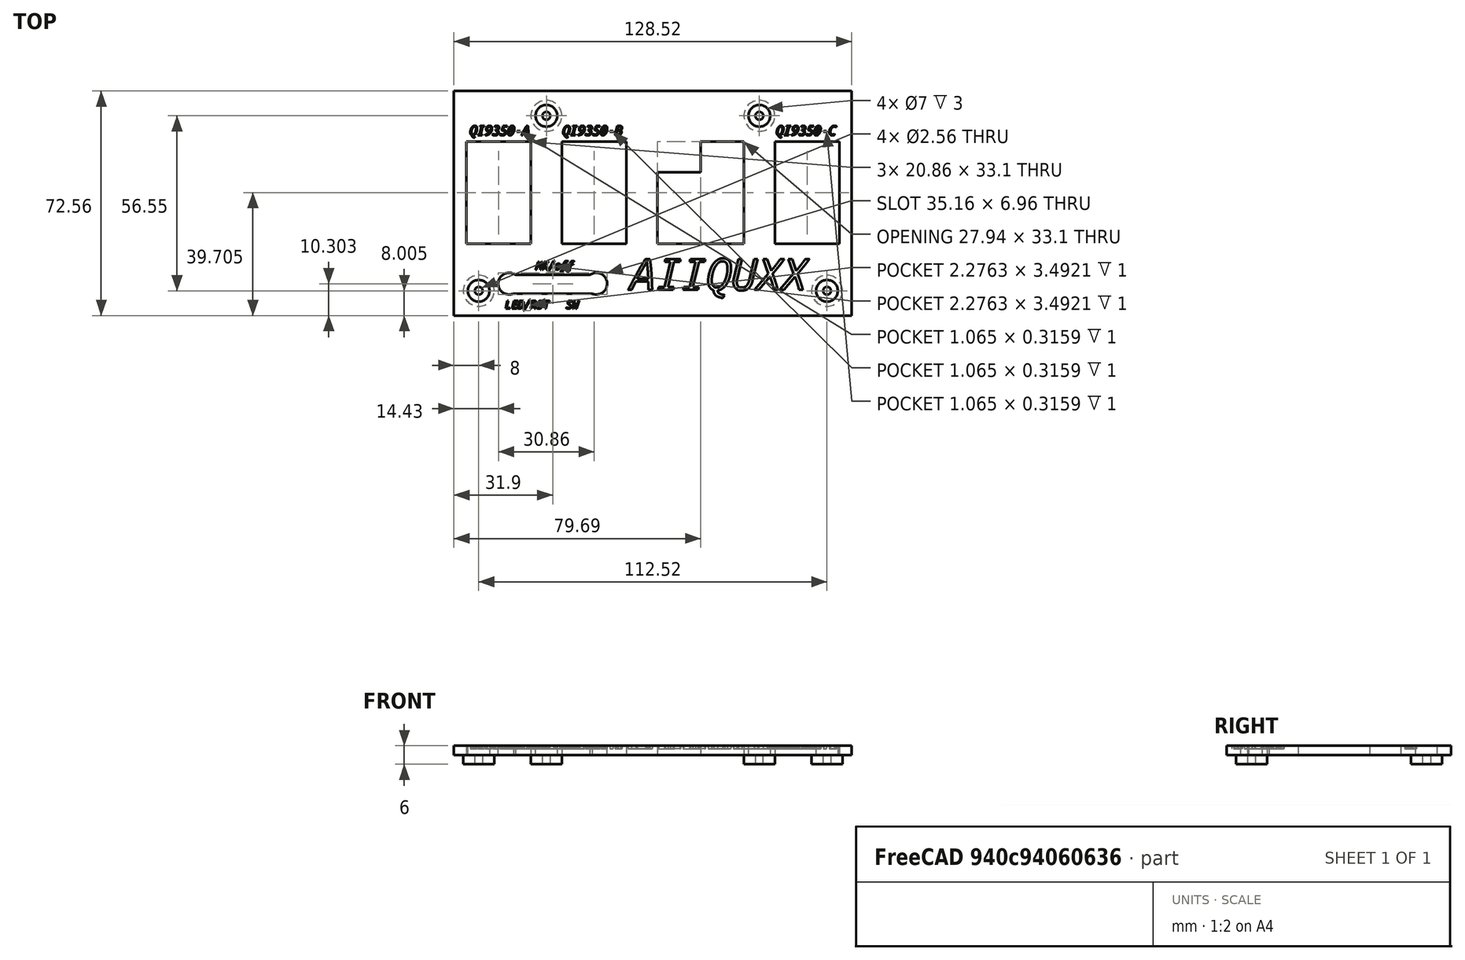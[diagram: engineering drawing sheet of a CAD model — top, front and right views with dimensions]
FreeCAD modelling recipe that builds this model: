
FCSTD DOCUMENT  (FreeCAD 1.0R38641 +678 (Git))
Label: box_cover_1
License: All rights reserved
LicenseURL: https://en.wikipedia.org/wiki/All_rights_reserved
objects: PartDesign::Pocket×9, Part::Part2DObjectPython×7, Sketcher::SketchObject×4, PartDesign::Pad×2, PartDesign::CoordinateSystem×1, PartDesign::Body×1, Mesh::Feature×1
note: 50 computed .brp shape members not serialized (recipe doc carries the construction recipe); baked Part::Feature solids carry a one-line shape summary decoded from their .brp

FEATURE [Sketcher::SketchObject] Sketch
  ArcFitTolerance = 1e-06
  AttachmentSupport = -> [XY_Plane]
  FullyConstrained = true
  MakeInternals = false
  MapMode = 5
  sketch-geometry (4):
    g0: LineSegment StartX=-64.26 StartY=-36.275 StartZ=0 EndX=64.26 EndY=-36.275 EndZ=0
    g1: LineSegment StartX=64.26 StartY=-36.275 StartZ=0 EndX=64.26 EndY=36.275 EndZ=0
    g2: LineSegment StartX=64.26 StartY=36.275 StartZ=0 EndX=-64.26 EndY=36.275 EndZ=0
    g3: LineSegment StartX=-64.26 StartY=36.275 StartZ=0 EndX=-64.26 EndY=-36.275 EndZ=0
  constraints (12):
    c: Coincident(g0,g1)
    c: Coincident(g1,g2)
    c: Coincident(g2,g3)
    c: Coincident(g3,g0)
    c: Horizontal(g0)
    c: Horizontal(g2)
    c: Vertical(g1)
    c: Vertical(g3)
    c: DistanceX(g2,g2) = 128.52
    c: DistanceX(g-1,g1) = 64.26
    c: DistanceY(g0,g1) = 72.55
    c: DistanceY(g0,g-1) = 36.275
FEATURE [PartDesign::Pad] Pad
  Direction = (0,0,1)
  Length = 3
  Length2 = 10
  Profile = -> Sketch
  ReferenceAxis = -> Sketch [N_Axis]
  Refine = true
  Suppressed = false
  Type = 0
FEATURE [Sketcher::SketchObject] Sketch001
  ArcFitTolerance = 1e-06
  AttachmentSupport = -> [Pad]
  ExternalGeometry = -> [Pad]
  FullyConstrained = true
  MakeInternals = false
  MapMode = 5
  Placement = pos=(0,0,3) rot=(0,0,1;0rad)
  sketch-geometry (30):
    g0: LineSegment StartX=-42.46 StartY=-29.175 StartZ=0 EndX=-22.2577 EndY=-29.175 EndZ=0
    g1: LineSegment StartX=-22.26 StartY=-23.175 StartZ=0 EndX=-42.46 EndY=-23.175 EndZ=0
    g2: Circle CenterX=-34.4 CenterY=28.275 CenterZ=0 NormalX=0 NormalY=0 NormalZ=1 AngleXU=0 Radius=3.5
    g3: Circle CenterX=34.4 CenterY=28.275 CenterZ=0 NormalX=0 NormalY=0 NormalZ=1 AngleXU=0 Radius=3.5
    g4: Circle CenterX=-56.26 CenterY=-28.275 CenterZ=0 NormalX=0 NormalY=0 NormalZ=1 AngleXU=0 Radius=3.5
    g5: Circle CenterX=56.26 CenterY=-28.275 CenterZ=0 NormalX=0 NormalY=0 NormalZ=1 AngleXU=0 Radius=3.5
    g6: ArcOfCircle CenterX=-46.46 CenterY=-25.975 CenterZ=0 NormalX=0 NormalY=0 NormalZ=1 AngleXU=0 Radius=3.5 StartAngle=0.927295 EndAngle=5.12944
    g7: ArcOfCircle CenterX=-18.26 CenterY=-25.975 CenterZ=0 NormalX=0 NormalY=0 NormalZ=1 AngleXU=0 Radius=3.5 StartAngle=4.29533 EndAngle=8.49748
    g8: LineSegment StartX=-42.46 StartY=-23.175 StartZ=0 EndX=-44.36 EndY=-23.175 EndZ=0
    g9: LineSegment StartX=-42.46 StartY=-29.175 StartZ=0 EndX=-45.0423 EndY=-29.175 EndZ=0
    g10: LineSegment StartX=-22.26 StartY=-23.175 StartZ=0 EndX=-20.36 EndY=-23.175 EndZ=0
    g11: LineSegment StartX=-22.2577 StartY=-29.175 StartZ=0 EndX=-19.6777 EndY=-29.175 EndZ=0
    g12: LineSegment StartX=-60.26 StartY=-13.125 StartZ=0 EndX=-39.4 EndY=-13.125 EndZ=0
    g13: LineSegment StartX=-39.4 StartY=-13.125 StartZ=0 EndX=-39.4 EndY=19.975 EndZ=0
    g14: LineSegment StartX=-39.4 StartY=19.975 StartZ=0 EndX=-60.26 EndY=19.975 EndZ=0
    g15: LineSegment StartX=-60.26 StartY=19.975 StartZ=0 EndX=-60.26 EndY=-13.125 EndZ=0
    g16: LineSegment StartX=-29.4 StartY=-13.125 StartZ=0 EndX=-8.54 EndY=-13.125 EndZ=0
    g17: LineSegment StartX=-8.54 StartY=-13.125 StartZ=0 EndX=-8.54 EndY=19.975 EndZ=0
    g18: LineSegment StartX=-8.54 StartY=19.975 StartZ=0 EndX=-29.4 EndY=19.975 EndZ=0
    g19: LineSegment StartX=-29.4 StartY=19.975 StartZ=0 EndX=-29.4 EndY=-13.125 EndZ=0
    g20: LineSegment StartX=39.4 StartY=-13.125 StartZ=0 EndX=60.26 EndY=-13.125 EndZ=0
    g21: LineSegment StartX=60.26 StartY=-13.125 StartZ=0 EndX=60.26 EndY=19.975 EndZ=0
    g22: LineSegment StartX=60.26 StartY=19.975 StartZ=0 EndX=39.4 EndY=19.975 EndZ=0
    g23: LineSegment StartX=39.4 StartY=19.975 StartZ=0 EndX=39.4 EndY=-13.125 EndZ=0
    g24: LineSegment StartX=1.46 StartY=9.975 StartZ=0 EndX=1.46 EndY=-13.125 EndZ=0
    g25: LineSegment StartX=1.46 StartY=-13.125 StartZ=0 EndX=29.4 EndY=-13.125 EndZ=0
    g26: LineSegment StartX=29.4 StartY=-13.125 StartZ=0 EndX=29.4 EndY=19.975 EndZ=0
    g27: LineSegment StartX=29.4 StartY=19.975 StartZ=0 EndX=15.46 EndY=19.975 EndZ=0
    g28: LineSegment StartX=1.46 StartY=9.975 StartZ=0 EndX=15.46 EndY=9.975 EndZ=0
    g29: LineSegment StartX=15.46 StartY=9.975 StartZ=0 EndX=15.46 EndY=19.975 EndZ=0
  constraints (95):
    c: Horizontal(g0)
    c: Horizontal(g1)
    c: DistanceX(g1,g1) = 20.2
    c: DistanceX(g-3,g0) = 21.8
    c: DistanceY(g0,g1) = 6
    c: DistanceY(g-3,g0) = 7.1
    c: Radius(g2) = 3.5
    c: Equal(g2,g3)
    c: Equal(g3,g5)
    c: Equal(g5,g4)
    c: DistanceX(g-3,g4) = 8
    c: DistanceX(g5,g-4) = 8
    c: DistanceY(g-3,g4) = 8
    c: DistanceY(g-4,g5) = 8
    c: DistanceY(g2,g-3) = 8
    c: DistanceY(g3,g-4) = 8
    c: DistanceX(g-3,g2) = 29.86
    c: DistanceX(g3,g-4) = 29.86
    c: Equal(g2,g7)
    c: Equal(g7,g6)
    c: DistanceX(g-3,g6) = 17.8
    c: DistanceY(g-3,g6) = 10.3
    c: DistanceY(g6,g7) = 0
    c: DistanceX(g-3,g7) = 46
    c: Coincident(g8,g1)
    c: Horizontal(g8)
    c: Coincident(g9,g0)
    c: Horizontal(g9)
    c: Coincident(g6,g9)
    c: Coincident(g6,g8)
    c: Horizontal(g10)
    c: Coincident(g11,g0)
    c: Horizontal(g11)
    c: Coincident(g7,g10)
    c: Coincident(g7,g11)
    c: DistanceX(g10,g10) = 1.9
    c: DistanceX(g11,g11) = 2.58
    c: DistanceX(g8,g8) = 1.9
    c: DistanceY(g1,g7) = 0
    c: Coincident(g12,g13)
    c: Coincident(g13,g14)
    c: Coincident(g14,g15)
    c: Coincident(g15,g12)
    c: Horizontal(g12)
    c: Horizontal(g14)
    c: Vertical(g13)
    c: Vertical(g15)
    c: Coincident(g16,g17)
    c: Coincident(g17,g18)
    c: Coincident(g18,g19)
    c: Coincident(g19,g16)
    c: Horizontal(g16)
    c: Horizontal(g18)
    c: Vertical(g17)
    c: Vertical(g19)
    c: Coincident(g20,g21)
    c: Coincident(g21,g22)
    c: Coincident(g22,g23)
    c: Coincident(g23,g20)
    c: Horizontal(g20)
    c: Horizontal(g22)
    c: Vertical(g21)
    c: Vertical(g23)
    c: Equal(g14,g18)
    c: Equal(g18,g22)
    c: Equal(g15,g19)
    c: DistanceY(g15,g15) = 33.1
    c: DistanceY(g18,g13) = 0
    c: DistanceX(g14,g14) = 20.86
    c: DistanceX(g-3,g14) = 4
    c: DistanceX(g21,g-4) = 4
    c: DistanceX(g13,g18) = 10
    c: DistanceY(g14,g-3) = 16.3
    c: DistanceY(g17,g22) = 0
    c: Equal(g19,g21)
    c: Coincident(g24,g25)
    c: Coincident(g25,g26)
    c: Coincident(g26,g27)
    c: Vertical(g24)
    c: Vertical(g26)
    c: Horizontal(g25)
    c: Horizontal(g27)
    c: Horizontal(g28)
    c: Coincident(g29,g28)
    c: Vertical(g29)
    c: DistanceY(g29,g26) = 0
    c: DistanceX(g24,g28) = 0
    c: PointOnObject(g27,g29)
    c: PointOnObject(g24,g28)
    c: DistanceX(g28,g28) = 14
    c: DistanceY(g29,g29) = 10
    c: DistanceY(g26,g22) = 0
    c: Equal(g26,g23)
    c: DistanceX(g16,g24) = 10
    c: DistanceX(g25,g20) = 10
FEATURE [PartDesign::Pocket] Pocket
  BaseFeature = -> Pad
  Direction = (0,0,-1)
  Length = 3
  Length2 = 5
  Profile = -> Sketch001
  ReferenceAxis = -> Sketch001 [N_Axis]
  Refine = true
  Suppressed = false
  Type = 0
FEATURE [Sketcher::SketchObject] Sketch002
  ArcFitTolerance = 1e-06
  AttachmentSupport = -> [Pocket]
  ExternalGeometry = -> [Pocket]
  FullyConstrained = true
  MakeInternals = false
  MapMode = 5
  Placement = pos=(0,0,0) rot=(1,0,0;3.14159rad)
  sketch-geometry (4):
    g0: Circle CenterX=-56.26 CenterY=28.275 CenterZ=0 NormalX=0 NormalY=0 NormalZ=1 AngleXU=0 Radius=5
    g1: Circle CenterX=56.26 CenterY=28.275 CenterZ=0 NormalX=0 NormalY=0 NormalZ=1 AngleXU=0 Radius=5
    g2: Circle CenterX=34.4 CenterY=-28.275 CenterZ=0 NormalX=0 NormalY=0 NormalZ=1 AngleXU=0 Radius=5
    g3: Circle CenterX=-34.4 CenterY=-28.275 CenterZ=0 NormalX=0 NormalY=0 NormalZ=1 AngleXU=0 Radius=5
  constraints (8):
    c: Radius(g0) = 5
    c: Equal(g0,g1)
    c: Equal(g1,g2)
    c: Equal(g2,g3)
    c: Coincident(g0,g-3)
    c: Coincident(g1,g-4)
    c: Coincident(g2,g-5)
    c: Coincident(g3,g-6)
FEATURE [PartDesign::Pad] Pad001
  BaseFeature = -> Pocket
  Direction = (0,0,-1)
  Length = 3
  Length2 = 10
  Profile = -> Sketch002
  ReferenceAxis = -> Sketch002 [N_Axis]
  Refine = true
  Suppressed = false
  Type = 0
FEATURE [Sketcher::SketchObject] Sketch003
  ArcFitTolerance = 1e-06
  AttachmentSupport = -> [Pad001]
  ExternalGeometry = -> [Pad001]
  FullyConstrained = true
  MakeInternals = false
  MapMode = 5
  Placement = pos=(0,0,-3) rot=(1,0,0;3.14159rad)
  sketch-geometry (4):
    g0: Circle CenterX=-56.26 CenterY=28.275 CenterZ=0 NormalX=0 NormalY=0 NormalZ=1 AngleXU=0 Radius=1.28
    g1: Circle CenterX=56.26 CenterY=28.275 CenterZ=0 NormalX=0 NormalY=0 NormalZ=1 AngleXU=0 Radius=1.28
    g2: Circle CenterX=34.4 CenterY=-28.275 CenterZ=0 NormalX=0 NormalY=0 NormalZ=1 AngleXU=0 Radius=1.28
    g3: Circle CenterX=-34.4 CenterY=-28.275 CenterZ=0 NormalX=0 NormalY=0 NormalZ=1 AngleXU=0 Radius=1.28
  constraints (8):
    c: Radius(g0) = 1.28
    c: Equal(g0,g1)
    c: Equal(g1,g2)
    c: Equal(g2,g3)
    c: Coincident(g0,g-3)
    c: Coincident(g1,g-4)
    c: Coincident(g2,g-5)
    c: Coincident(g3,g-6)
FEATURE [PartDesign::Pocket] Pocket001
  BaseFeature = -> Pad001
  Direction = (0,0,1)
  Length = 3
  Length2 = 5
  Profile = -> Sketch003
  ReferenceAxis = -> Sketch003 [N_Axis]
  Refine = true
  Suppressed = false
  Type = 0
FEATURE [PartDesign::CoordinateSystem] Local_CS
  AttacherType = Attacher::AttachEngine3D
  MapMode = 2
FEATURE [Part::Part2DObjectPython] ShapeString  # Draft 2D object (typed FeaturePython)
  FontFile = <path>
  Fuse = false
  Justification = 6
  JustificationReference = 0
  KeepLeftMargin = false
  MakeFace = true
  ObliqueAngle = 0
  Placement = pos=(-37.88,-21.41,3) rot=(0,0,1;0rad)
  ScaleToSize = true
  Size = 2.5
  String = MK/off
  Tracking = 0
FEATURE [Part::Part2DObjectPython] ShapeString001  # Draft 2D object (typed FeaturePython)
  FontFile = <path>
  Fuse = false
  Justification = 6
  JustificationReference = 0
  KeepLeftMargin = false
  MakeFace = true
  ObliqueAngle = 0
  Placement = pos=(-47.59,-34,3) rot=(0,0,1;0rad)
  ScaleToSize = true
  Size = 2.5
  String = LED/RST
  Tracking = 0
FEATURE [Part::Part2DObjectPython] ShapeString002  # Draft 2D object (typed FeaturePython)
  FontFile = <path>
  Fuse = false
  Justification = 6
  JustificationReference = 0
  KeepLeftMargin = false
  MakeFace = true
  ObliqueAngle = 0
  Placement = pos=(-28,-34,3) rot=(0,0,1;0rad)
  ScaleToSize = true
  Size = 2.5
  String = SW
  Tracking = 0
FEATURE [Part::Part2DObjectPython] ShapeString003  # Draft 2D object (typed FeaturePython)
  FontFile = <path>
  Fuse = false
  Justification = 6
  JustificationReference = 0
  KeepLeftMargin = false
  MakeFace = true
  ObliqueAngle = 0
  Placement = pos=(-59,22,3) rot=(0,0,1;0rad)
  ScaleToSize = true
  Size = 3
  String = QI9350-A
  Tracking = 0
FEATURE [Part::Part2DObjectPython] ShapeString004  # Draft 2D object (typed FeaturePython)
  FontFile = <path>
  Fuse = false
  Justification = 6
  JustificationReference = 0
  KeepLeftMargin = false
  MakeFace = true
  ObliqueAngle = 0
  Placement = pos=(-29,22,3) rot=(0,0,1;0rad)
  ScaleToSize = true
  Size = 3
  String = QI9350-B
  Tracking = 0
FEATURE [Part::Part2DObjectPython] ShapeString005  # Draft 2D object (typed FeaturePython)
  FontFile = <path>
  Fuse = false
  Justification = 6
  JustificationReference = 0
  KeepLeftMargin = false
  MakeFace = true
  ObliqueAngle = 0
  Placement = pos=(40,22,3) rot=(0,0,1;0rad)
  ScaleToSize = true
  Size = 3
  String = QI9350-C
  Tracking = 0
FEATURE [PartDesign::Pocket] Pocket002
  BaseFeature = -> Pocket001
  Direction = (0,0,-1)
  Length = 1
  Length2 = 5
  Profile = -> ShapeString
  ReferenceAxis = -> ShapeString [N_Axis]
  Refine = true
  Suppressed = false
  Type = 0
FEATURE [PartDesign::Pocket] Pocket003
  BaseFeature = -> Pocket002
  Direction = (0,0,-1)
  Length = 1
  Length2 = 5
  Profile = -> ShapeString001
  ReferenceAxis = -> ShapeString001 [N_Axis]
  Refine = true
  Suppressed = false
  Type = 0
FEATURE [PartDesign::Pocket] Pocket004
  BaseFeature = -> Pocket003
  Direction = (0,0,-1)
  Length = 1
  Length2 = 5
  Profile = -> ShapeString002
  ReferenceAxis = -> ShapeString002 [N_Axis]
  Refine = true
  Suppressed = false
  Type = 0
FEATURE [PartDesign::Pocket] Pocket005
  BaseFeature = -> Pocket004
  Direction = (0,0,-1)
  Length = 1
  Length2 = 5
  Profile = -> ShapeString003
  ReferenceAxis = -> ShapeString003 [N_Axis]
  Refine = true
  Suppressed = false
  Type = 0
FEATURE [PartDesign::Pocket] Pocket006
  BaseFeature = -> Pocket005
  Direction = (0,0,-1)
  Length = 1
  Length2 = 5
  Profile = -> ShapeString004
  ReferenceAxis = -> ShapeString004 [N_Axis]
  Refine = true
  Suppressed = false
  Type = 0
FEATURE [PartDesign::Pocket] Pocket007
  BaseFeature = -> Pocket006
  Direction = (0,0,-1)
  Length = 1
  Length2 = 5
  Profile = -> ShapeString005
  ReferenceAxis = -> ShapeString005 [N_Axis]
  Refine = true
  Suppressed = false
  Type = 0
FEATURE [Part::Part2DObjectPython] ShapeString006  # Draft 2D object (typed FeaturePython)
  FontFile = <path>
  Fuse = false
  Justification = 6
  JustificationReference = 0
  KeepLeftMargin = false
  MakeFace = true
  ObliqueAngle = 0
  Placement = pos=(-8,-28,3) rot=(0,0,1;0rad)
  ScaleToSize = true
  Size = 10
  String = AIIQUXX
  Tracking = 0
FEATURE [PartDesign::Pocket] Pocket008
  BaseFeature = -> Pocket007
  Direction = (0,0,-1)
  Length = 1
  Length2 = 5
  Profile = -> ShapeString006
  ReferenceAxis = -> ShapeString006 [N_Axis]
  Refine = true
  Suppressed = false
  Type = 0
FEATURE [PartDesign::Body] Body
  AllowCompound = false
  Group = -> [Sketch,Pad,Sketch001,Pocket,Sketch002,Pad001,Sketch003,Pocket001,Local_CS,ShapeString,Pocket002,ShapeString001,ShapeString002,ShapeString003,ShapeString004,ShapeString005,Pocket003,Pocket004,Pocket005,Pocket006,Pocket007,ShapeString006,Pocket008]
  Origin = -> Origin
  Tip = -> Pocket008
FEATURE [Mesh::Feature] Mesh  label="Pocket008 (Meshed)"
note: 7 file-system paths scrubbed to <path> (originals preserved in the JSON sidecar)
